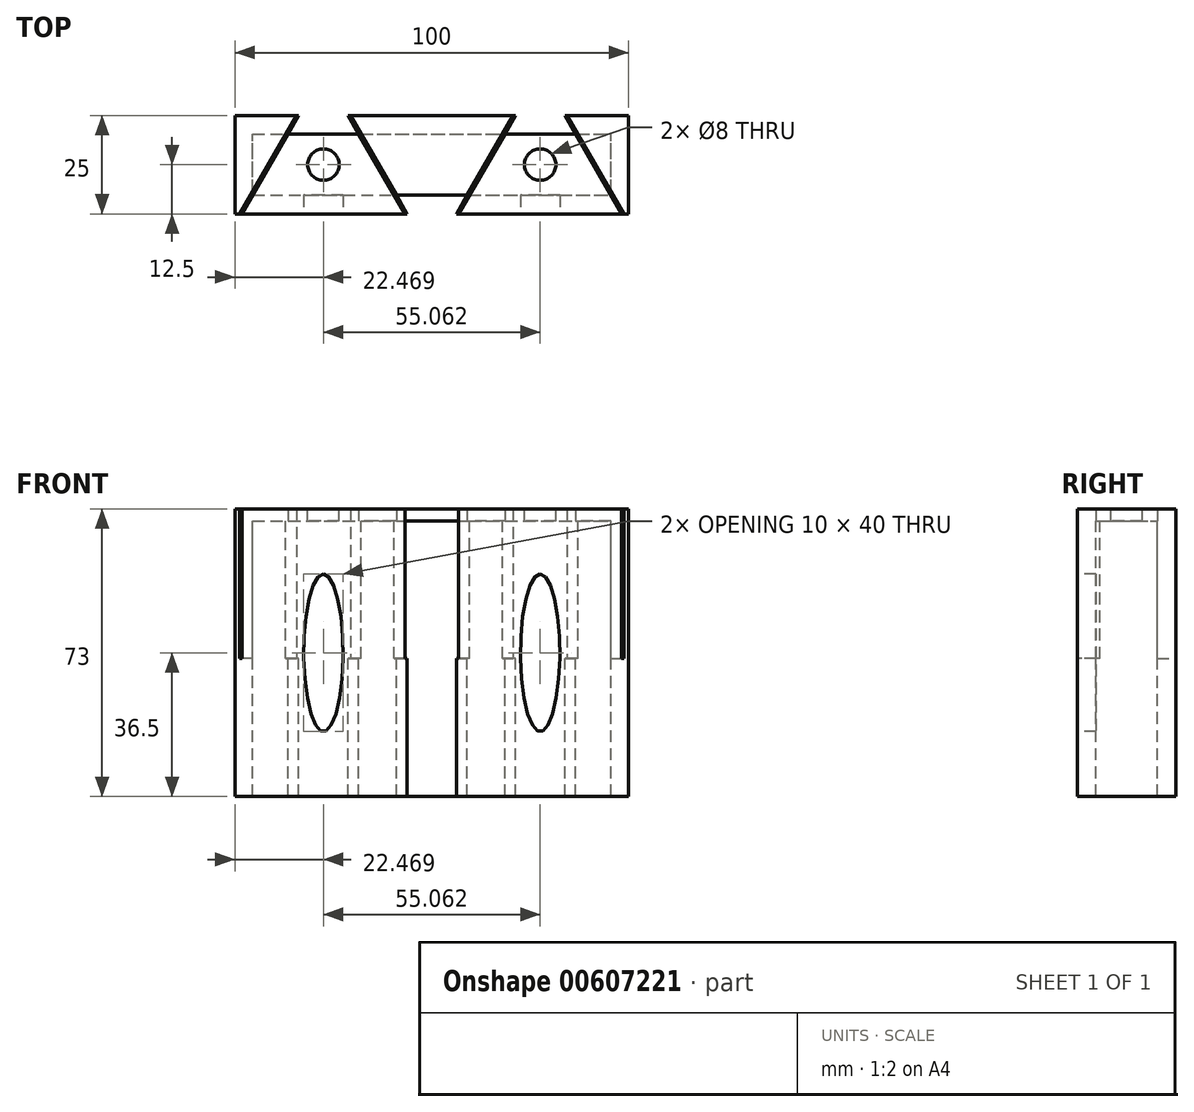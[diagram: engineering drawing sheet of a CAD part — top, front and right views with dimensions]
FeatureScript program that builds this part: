
annotation { "Feature Type Name" : "Feature", "Feature Type Description" : "" }
export const myFeature = defineFeature(function(context is Context, id is Id, definition is map)
    precondition{}
    {
        {
            var Q0;
            Q0=qCreatedBy(makeId("Top.planeOp"),FACE);
            var sketch = newSketch(context, id + "F0", { "sketchPlane" : qUnion([Q0])});
            skLineSegment(sketch, "E0.bottom", {"start": v(-45.5, -7.78) * mm, "end": v(45.5, -7.78) * mm});
            skLineSegment(sketch, "E0.top", {"start": v(-45.5, 7.78) * mm, "end": v(45.5, 7.78) * mm});
            skLineSegment(sketch, "E0.left", {"start": v(-45.5, -7.78) * mm, "end": v(-45.5, 7.78) * mm});
            skLineSegment(sketch, "E0.right", {"start": v(45.5, -7.78) * mm, "end": v(45.5, 7.78) * mm});
            skPoint(sketch, "E0.middle", {"position": v(0, 0) * mm});
            skLineSegment(sketch, "E1", {"start": v(-45.5, -7.78) * mm, "end": v(-36.52, 7.78) * mm});
            skLineSegment(sketch, "E2", {"start": v(-45.5, -6.78) * mm, "end": v(-37.1, 7.78) * mm});
            skLineSegment(sketch, "E3", {"start": v(-9.56, -7.78) * mm, "end": v(-18.55, 7.78) * mm});
            skLineSegment(sketch, "E4", {"start": v(-8.98, -7.78) * mm, "end": v(-17.97, 7.78) * mm});
            skLineSegment(sketch, "E5", {"start": v(8.98, -7.78) * mm, "end": v(17.97, 7.78) * mm});
            skLineSegment(sketch, "E6", {"start": v(9.56, -7.78) * mm, "end": v(18.55, 7.78) * mm});
            skLineSegment(sketch, "E7", {"start": v(45.5, -7.78) * mm, "end": v(36.52, 7.78) * mm});
            skLineSegment(sketch, "E8", {"start": v(45.5, -6.78) * mm, "end": v(37.1, 7.78) * mm});
            skLineSegment(sketch, "E9", {"start": v(-36.52, 7.78) * mm, "end": v(-18.55, 7.78) * mm});
            skLineSegment(sketch, "E10", {"start": v(-8.98, -7.78) * mm, "end": v(8.98, -7.78) * mm});
            skLineSegment(sketch, "E11", {"start": v(18.55, 7.78) * mm, "end": v(36.52, 7.78) * mm});
            skLineSegment(sketch, "E12.bottom", {"start": v(-50, -12.5) * mm, "end": v(50, -12.5) * mm});
            skLineSegment(sketch, "E12.top", {"start": v(-50, 12.5) * mm, "end": v(50, 12.5) * mm});
            skLineSegment(sketch, "E12.left", {"start": v(-50, -12.5) * mm, "end": v(-50, 12.5) * mm});
            skLineSegment(sketch, "E12.right", {"start": v(50, -12.5) * mm, "end": v(50, 12.5) * mm});
            skLineSegment(sketch, "E13", {"start": v(-45.5, -6.78) * mm, "end": v(-48.8, -12.5) * mm});
            skLineSegment(sketch, "E14", {"start": v(-45.5, -7.78) * mm, "end": v(-48.22, -12.5) * mm});
            skLineSegment(sketch, "E15", {"start": v(-37.1, 7.78) * mm, "end": v(-34.37, 12.5) * mm});
            skLineSegment(sketch, "E16", {"start": v(-36.52, 7.78) * mm, "end": v(-33.8, 12.5) * mm});
            skLineSegment(sketch, "E17", {"start": v(-18.55, 7.78) * mm, "end": v(-21.27, 12.5) * mm});
            skLineSegment(sketch, "E18", {"start": v(-17.97, 7.78) * mm, "end": v(-20.7, 12.5) * mm});
            skLineSegment(sketch, "E19", {"start": v(-9.56, -7.78) * mm, "end": v(-6.84, -12.5) * mm});
            skLineSegment(sketch, "E20", {"start": v(-8.98, -7.78) * mm, "end": v(-6.26, -12.5) * mm});
            skLineSegment(sketch, "E21", {"start": v(17.97, 7.78) * mm, "end": v(20.7, 12.5) * mm});
            skLineSegment(sketch, "E22", {"start": v(18.55, 7.78) * mm, "end": v(21.27, 12.5) * mm});
            skLineSegment(sketch, "E23", {"start": v(8.98, -7.78) * mm, "end": v(6.26, -12.5) * mm});
            skLineSegment(sketch, "E24", {"start": v(9.56, -7.78) * mm, "end": v(6.84, -12.5) * mm});
            skLineSegment(sketch, "E25", {"start": v(36.52, 7.78) * mm, "end": v(33.8, 12.5) * mm});
            skLineSegment(sketch, "E26", {"start": v(37.1, 7.78) * mm, "end": v(34.37, 12.5) * mm});
            skLineSegment(sketch, "E27", {"start": v(45.5, -7.78) * mm, "end": v(48.22, -12.5) * mm});
            skLineSegment(sketch, "E28", {"start": v(45.5, -6.78) * mm, "end": v(48.8, -12.5) * mm});
            skSolve(sketch);
        }
        {
            var Q0;
            Q0=makeQuery(id+"F0.imprint","IMPRINT",FACE,{"disambiguationData":[TD([[makeQuery(id+"F0.imprint","IMPRINT",EDGE,{"derivedFrom":sQuery(id+"F0.wireOp",EDGE,"E10")}),-1.0]])]});
            var Q1;
            {var subQ3=sQuery(id+"F0.wireOp",EDGE,"E2");Q1=makeQuery(id+"F0.imprint","IMPRINT",FACE,{"disambiguationData":[TD([[makeQuery(id+"F0.imprint","IMPRINT",EDGE,{"derivedFrom":subQ3}),1.0]])]});}
            var Q2;
            {var subQ3=sQuery(id+"F0.wireOp",EDGE,"E8");Q2=makeQuery(id+"F0.imprint","IMPRINT",FACE,{"disambiguationData":[TD([[makeQuery(id+"F0.imprint","IMPRINT",EDGE,{"derivedFrom":subQ3}),-1.0]])]});}
            var Q3;
            Q3=makeQuery(id+"F0.imprint","IMPRINT",FACE,{"disambiguationData":[TD([[makeQuery(id+"F0.imprint","IMPRINT",EDGE,{"derivedFrom":sQuery(id+"F0.wireOp",EDGE,"E11")}),1.0]])]});
            var Q4;
            {var subQ2=sQuery(id+"F0.wireOp",EDGE,"E24");Q4=makeQuery(id+"F0.imprint","IMPRINT",FACE,{"disambiguationData":[TD([[makeQuery(id+"F0.imprint","IMPRINT",EDGE,{"derivedFrom":subQ2}),1.0]])]});}
            var Q5;
            {var subQ0=sQuery(id+"F0.wireOp",EDGE,"E12.left");Q5=makeQuery(id+"F0.imprint","IMPRINT",FACE,{"disambiguationData":[TD([[makeQuery(id+"F0.imprint","IMPRINT",EDGE,{"derivedFrom":subQ0}),-1.0]])]});}
            var Q6;
            {var subQ0=sQuery(id+"F0.wireOp",EDGE,"E18");Q6=makeQuery(id+"F0.imprint","IMPRINT",FACE,{"disambiguationData":[TD([[makeQuery(id+"F0.imprint","IMPRINT",EDGE,{"derivedFrom":subQ0}),-1.0]])]});}
            var Q7;
            {var subQ0=sQuery(id+"F0.wireOp",EDGE,"E12.right");Q7=makeQuery(id+"F0.imprint","IMPRINT",FACE,{"disambiguationData":[TD([[makeQuery(id+"F0.imprint","IMPRINT",EDGE,{"derivedFrom":subQ0}),1.0]])]});}
            var Q8;
            {var subQ0=sQuery(id+"F0.wireOp",EDGE,"E4");Q8=makeQuery(id+"F0.imprint","IMPRINT",FACE,{"disambiguationData":[TD([[makeQuery(id+"F0.imprint","IMPRINT",EDGE,{"derivedFrom":subQ0}),-1.0]])]});}
            var Q9;
            {var subQ2=sQuery(id+"F0.wireOp",EDGE,"E6");Q9=makeQuery(id+"F0.imprint","IMPRINT",FACE,{"disambiguationData":[TD([[makeQuery(id+"F0.imprint","IMPRINT",EDGE,{"derivedFrom":subQ2}),-1.0]])]});}
            var Q10;
            {var subQ0=sQuery(id+"F0.wireOp",EDGE,"E1");Q10=makeQuery(id+"F0.imprint","IMPRINT",FACE,{"disambiguationData":[TD([[makeQuery(id+"F0.imprint","IMPRINT",EDGE,{"derivedFrom":subQ0}),-1.0]])]});}
            var Q11;
            Q11=makeQuery(id+"F0.imprint","IMPRINT",FACE,{"disambiguationData":[TD([[makeQuery(id+"F0.imprint","IMPRINT",EDGE,{"derivedFrom":sQuery(id+"F0.wireOp",EDGE,"E9")}),1.0]])]});
            var Q12;
            {var subQ0=sQuery(id+"F0.wireOp",EDGE,"E14");Q12=makeQuery(id+"F0.imprint","IMPRINT",FACE,{"disambiguationData":[TD([[makeQuery(id+"F0.imprint","IMPRINT",EDGE,{"derivedFrom":subQ0}),1.0]])]});}
            extrude(context, id + "F1", {"entities" : qUnion([Q0, Q1, Q2, Q3, Q4, Q5, Q6, Q7, Q8, Q9, Q10, Q11, Q12]), "depth" : 3 * mm, "offsetDistance" : 25 * mm});
        }
        {
            var Q0;
            {var subQ0=sQuery(id+"F0.wireOp",EDGE,"E12.left");Q0=makeQuery(id+"F0.imprint","IMPRINT",FACE,{"disambiguationData":[TD([[makeQuery(id+"F0.imprint","IMPRINT",EDGE,{"derivedFrom":subQ0}),-1.0]])]});}
            var Q1;
            {var subQ0=sQuery(id+"F0.wireOp",EDGE,"E14");Q1=makeQuery(id+"F0.imprint","IMPRINT",FACE,{"disambiguationData":[TD([[makeQuery(id+"F0.imprint","IMPRINT",EDGE,{"derivedFrom":subQ0}),1.0]])]});}
            var Q2;
            {var subQ0=sQuery(id+"F0.wireOp",EDGE,"E18");Q2=makeQuery(id+"F0.imprint","IMPRINT",FACE,{"disambiguationData":[TD([[makeQuery(id+"F0.imprint","IMPRINT",EDGE,{"derivedFrom":subQ0}),-1.0]])]});}
            var Q3;
            Q3=makeQuery(id+"F0.imprint","IMPRINT",FACE,{"disambiguationData":[TD([[makeQuery(id+"F0.imprint","IMPRINT",EDGE,{"derivedFrom":sQuery(id+"F0.wireOp",EDGE,"E10")}),-1.0]])]});
            var Q4;
            {var subQ2=sQuery(id+"F0.wireOp",EDGE,"E24");Q4=makeQuery(id+"F0.imprint","IMPRINT",FACE,{"disambiguationData":[TD([[makeQuery(id+"F0.imprint","IMPRINT",EDGE,{"derivedFrom":subQ2}),1.0]])]});}
            var Q5;
            Q5=makeQuery(id+"F0.imprint","IMPRINT",FACE,{"disambiguationData":[TD([[makeQuery(id+"F0.imprint","IMPRINT",EDGE,{"derivedFrom":sQuery(id+"F0.wireOp",EDGE,"E11")}),1.0]])]});
            var Q6;
            {var subQ0=sQuery(id+"F0.wireOp",EDGE,"E12.right");Q6=makeQuery(id+"F0.imprint","IMPRINT",FACE,{"disambiguationData":[TD([[makeQuery(id+"F0.imprint","IMPRINT",EDGE,{"derivedFrom":subQ0}),1.0]])]});}
            var Q7;
            Q7=makeQuery(id+"F0.imprint","IMPRINT",FACE,{"disambiguationData":[TD([[makeQuery(id+"F0.imprint","IMPRINT",EDGE,{"derivedFrom":sQuery(id+"F0.wireOp",EDGE,"E9")}),1.0]])]});
            extrude(context, id + "F2", {"entities" : qUnion([Q0, Q1, Q2, Q3, Q4, Q5, Q6, Q7]), "operationType" : NewBodyOperationType.ADD, "oppositeDirection" : true, "depth" : 35 * mm, "offsetDistance" : 25 * mm});
        }
        {
            var Q0;
            {var subQ0=sQuery(id+"F0.wireOp",EDGE,"E19");Q0=makeQuery(id+"F0.imprint","IMPRINT",FACE,{"disambiguationData":[TD([[makeQuery(id+"F0.imprint","IMPRINT",EDGE,{"derivedFrom":subQ0}),1.0]])]});}
            var Q1;
            Q1=makeQuery(id+"F0.imprint","IMPRINT",FACE,{"disambiguationData":[TD([[makeQuery(id+"F0.imprint","IMPRINT",EDGE,{"derivedFrom":sQuery(id+"F0.wireOp",EDGE,"E9")}),1.0]])]});
            var Q2;
            {var subQ2=sQuery(id+"F0.wireOp",EDGE,"E13");Q2=makeQuery(id+"F0.imprint","IMPRINT",FACE,{"disambiguationData":[TD([[makeQuery(id+"F0.imprint","IMPRINT",EDGE,{"derivedFrom":subQ2}),1.0]])]});}
            var Q3;
            {var subQ0=sQuery(id+"F0.wireOp",EDGE,"E27");Q3=makeQuery(id+"F0.imprint","IMPRINT",FACE,{"disambiguationData":[TD([[makeQuery(id+"F0.imprint","IMPRINT",EDGE,{"derivedFrom":subQ0}),1.0]])]});}
            var Q4;
            Q4=makeQuery(id+"F0.imprint","IMPRINT",FACE,{"disambiguationData":[TD([[makeQuery(id+"F0.imprint","IMPRINT",EDGE,{"derivedFrom":sQuery(id+"F0.wireOp",EDGE,"E10")}),-1.0]])]});
            var Q5;
            {var subQ0=sQuery(id+"F0.wireOp",EDGE,"E14");Q5=makeQuery(id+"F0.imprint","IMPRINT",FACE,{"disambiguationData":[TD([[makeQuery(id+"F0.imprint","IMPRINT",EDGE,{"derivedFrom":subQ0}),1.0]])]});}
            var Q6;
            {var subQ0=sQuery(id+"F0.wireOp",EDGE,"E23");Q6=makeQuery(id+"F0.imprint","IMPRINT",FACE,{"disambiguationData":[TD([[makeQuery(id+"F0.imprint","IMPRINT",EDGE,{"derivedFrom":subQ0}),1.0]])]});}
            var Q7;
            {var subQ2=sQuery(id+"F0.wireOp",EDGE,"E24");Q7=makeQuery(id+"F0.imprint","IMPRINT",FACE,{"disambiguationData":[TD([[makeQuery(id+"F0.imprint","IMPRINT",EDGE,{"derivedFrom":subQ2}),1.0]])]});}
            var Q8;
            {var subQ0=sQuery(id+"F0.wireOp",EDGE,"E12.left");Q8=makeQuery(id+"F0.imprint","IMPRINT",FACE,{"disambiguationData":[TD([[makeQuery(id+"F0.imprint","IMPRINT",EDGE,{"derivedFrom":subQ0}),-1.0]])]});}
            var Q9;
            {var subQ2=sQuery(id+"F0.wireOp",EDGE,"E15");Q9=makeQuery(id+"F0.imprint","IMPRINT",FACE,{"disambiguationData":[TD([[makeQuery(id+"F0.imprint","IMPRINT",EDGE,{"derivedFrom":subQ2}),-1.0]])]});}
            var Q10;
            {var subQ0=sQuery(id+"F0.wireOp",EDGE,"E17");Q10=makeQuery(id+"F0.imprint","IMPRINT",FACE,{"disambiguationData":[TD([[makeQuery(id+"F0.imprint","IMPRINT",EDGE,{"derivedFrom":subQ0}),-1.0]])]});}
            var Q11;
            {var subQ0=sQuery(id+"F0.wireOp",EDGE,"E18");Q11=makeQuery(id+"F0.imprint","IMPRINT",FACE,{"disambiguationData":[TD([[makeQuery(id+"F0.imprint","IMPRINT",EDGE,{"derivedFrom":subQ0}),-1.0]])]});}
            var Q12;
            {var subQ0=sQuery(id+"F0.wireOp",EDGE,"E21");Q12=makeQuery(id+"F0.imprint","IMPRINT",FACE,{"disambiguationData":[TD([[makeQuery(id+"F0.imprint","IMPRINT",EDGE,{"derivedFrom":subQ0}),-1.0]])]});}
            var Q13;
            {var subQ0=sQuery(id+"F0.wireOp",EDGE,"E25");Q13=makeQuery(id+"F0.imprint","IMPRINT",FACE,{"disambiguationData":[TD([[makeQuery(id+"F0.imprint","IMPRINT",EDGE,{"derivedFrom":subQ0}),-1.0]])]});}
            var Q14;
            {var subQ0=sQuery(id+"F0.wireOp",EDGE,"E12.right");Q14=makeQuery(id+"F0.imprint","IMPRINT",FACE,{"disambiguationData":[TD([[makeQuery(id+"F0.imprint","IMPRINT",EDGE,{"derivedFrom":subQ0}),1.0]])]});}
            var Q15;
            Q15=makeQuery(id+"F0.imprint","IMPRINT",FACE,{"disambiguationData":[TD([[makeQuery(id+"F0.imprint","IMPRINT",EDGE,{"derivedFrom":sQuery(id+"F0.wireOp",EDGE,"E11")}),1.0]])]});
            var Q16;
            Q16=makeQuery(id+"F2.opExtrude","CAP_FACE",FACE,{"disambiguationData":[OSD([sQuery(id+"F0.wireOp",EDGE,"E9"),sQuery(id+"F0.wireOp",EDGE,"E12.top"),sQuery(id+"F0.wireOp",EDGE,"E16"),sQuery(id+"F0.wireOp",EDGE,"E17")])],"isStart":false});
            extrude(context, id + "F3", {"entities" : qUnion([Q0, Q1, Q2, Q3, Q4, Q5, Q6, Q7, Q8, Q9, Q10, Q11, Q12, Q13, Q14, Q15]), "operationType" : NewBodyOperationType.ADD, "oppositeDirection" : true, "depth" : 70 * mm, "offsetDistance" : 25 * mm, "hasSecondDirection" : true, "secondDirectionBound" : SecondDirectionBoundingType.UP_TO_SURFACE, "secondDirectionOppositeDirection" : true, "secondDirectionDepth" : 25 * mm, "secondDirectionBoundEntityFace" : qUnion([Q16])});
        }
        {
            var Q0;
            {var subQ0=sQuery(id+"F0.wireOp",EDGE,"E12.bottom");var subQ1=makeQuery(id+"F0.imprint","IMPRINT",EDGE,{"disambiguationData":[TD([[makeQuery(id+"F0.imprint","INTERSECT",VERTEX,{"derivedFrom":[subQ0,sQuery(id+"F0.wireOp",EDGE,"E12.right")]}),1.0]])],"derivedFrom":subQ0});var subQ2=makeQuery(id+"F0.imprint","IMPRINT",EDGE,{"disambiguationData":[TD([[makeQuery(id+"F0.imprint","INTERSECT",VERTEX,{"derivedFrom":[subQ0,sQuery(id+"F0.wireOp",EDGE,"E24")]}),-1.0]])],"derivedFrom":subQ0});var subQ3=makeQuery(id+"F0.imprint","IMPRINT",EDGE,{"disambiguationData":[TD([[makeQuery(id+"F0.imprint","INTERSECT",VERTEX,{"derivedFrom":[subQ0,sQuery(id+"F0.wireOp",EDGE,"E20")]}),-1.0]])],"derivedFrom":subQ0});var subQ4=makeQuery(id+"F0.imprint","IMPRINT",EDGE,{"disambiguationData":[TD([[makeQuery(id+"F0.imprint","INTERSECT",VERTEX,{"derivedFrom":[subQ0,sQuery(id+"F0.wireOp",EDGE,"E14")]}),-1.0]])],"derivedFrom":subQ0});var subQ5=makeQuery(id+"F0.imprint","IMPRINT",EDGE,{"disambiguationData":[TD([[makeQuery(id+"F0.imprint","INTERSECT",VERTEX,{"derivedFrom":[subQ0,sQuery(id+"F0.wireOp",EDGE,"E12.left")]}),-1.0]])],"derivedFrom":subQ0});Q0=makeQuery(id+"F3.boolean.opBoolean","MERGE",FACE,{"derivedFrom":[makeQuery(id+"F2.boolean.opBoolean","MERGE",FACE,{"derivedFrom":[makeQuery(id+"F1.opExtrude","SWEPT_FACE",FACE,{"disambiguationData":[OSD([subQ0]),TDD([subQ5])]}),makeQuery(id+"F2.opExtrude","SWEPT_FACE",FACE,{"disambiguationData":[OSD([subQ0]),TDD([subQ5])]})]}),makeQuery(id+"F2.boolean.opBoolean","MERGE",FACE,{"derivedFrom":[makeQuery(id+"F1.opExtrude","SWEPT_FACE",FACE,{"disambiguationData":[OSD([subQ0]),TDD([subQ4])]}),makeQuery(id+"F2.opExtrude","SWEPT_FACE",FACE,{"disambiguationData":[OSD([subQ0]),TDD([subQ4])]})]}),makeQuery(id+"F2.boolean.opBoolean","MERGE",FACE,{"derivedFrom":[makeQuery(id+"F1.opExtrude","SWEPT_FACE",FACE,{"disambiguationData":[OSD([subQ0]),TDD([subQ3])]}),makeQuery(id+"F2.opExtrude","SWEPT_FACE",FACE,{"disambiguationData":[OSD([subQ0]),TDD([subQ3])]})]}),makeQuery(id+"F2.boolean.opBoolean","MERGE",FACE,{"derivedFrom":[makeQuery(id+"F1.opExtrude","SWEPT_FACE",FACE,{"disambiguationData":[OSD([subQ0]),TDD([subQ2])]}),makeQuery(id+"F2.opExtrude","SWEPT_FACE",FACE,{"disambiguationData":[OSD([subQ0]),TDD([subQ2])]})]}),makeQuery(id+"F2.boolean.opBoolean","MERGE",FACE,{"derivedFrom":[makeQuery(id+"F1.opExtrude","SWEPT_FACE",FACE,{"disambiguationData":[OSD([subQ0]),TDD([subQ1])]}),makeQuery(id+"F2.opExtrude","SWEPT_FACE",FACE,{"disambiguationData":[OSD([subQ0]),TDD([subQ1])]})]}),makeQuery(id+"F3.opExtrude","SWEPT_FACE",FACE,{"disambiguationData":[OSD([subQ0])]})]});}
            var sketch = newSketch(context, id + "F4", { "sketchPlane" : qUnion([Q0])});
            skLineSegment(sketch, "E29", {"start": v(-48.22, 3) * mm, "end": v(-6.84, -70) * mm, "construction": true});
            skEllipse(sketch, "E30", {"center": v(-27.53, -33.5) * mm, "majorRadius": 20 * mm, "minorRadius": 5 * mm, "majorAxis": v(0, 1)});
            skLineSegment(sketch, "E31", {"start": v(0, 3) * mm, "end": v(0, -70) * mm, "construction": true});
            skEllipse(sketch, "E32.MirrorC", {"center": v(27.53, -33.5) * mm, "majorRadius": 20 * mm, "minorRadius": 5 * mm, "majorAxis": v(0, 1)});
            skSolve(sketch);
        }
        {
            var Q0;
            Q0=makeQuery(id+"F4.imprint","IMPRINT",FACE,{"disambiguationData":[TD([[makeQuery(id+"F4.imprint","IMPRINT",EDGE,{"derivedFrom":sQuery(id+"F4.wireOp",EDGE,"E30")}),1.0]])]});
            var Q1;
            Q1=makeQuery(id+"F4.imprint","IMPRINT",FACE,{"disambiguationData":[TD([[makeQuery(id+"F4.imprint","IMPRINT",EDGE,{"derivedFrom":sQuery(id+"F4.wireOp",EDGE,"E32.MirrorC")}),1.0]])]});
            extrude(context, id + "F5", {"entities" : qUnion([Q0, Q1]), "operationType" : NewBodyOperationType.REMOVE, "endBound" : BoundingType.UP_TO_NEXT, "oppositeDirection" : true, "depth" : 25 * mm, "offsetDistance" : 25 * mm});
        }
        {
            var Q0;
            Q0=makeQuery(id+"F1.opExtrude","CAP_FACE",FACE,{"disambiguationData":[OSD([sQuery(id+"F0.wireOp",EDGE,"E1"),sQuery(id+"F0.wireOp",EDGE,"E3"),sQuery(id+"F0.wireOp",EDGE,"E12.bottom"),sQuery(id+"F0.wireOp",EDGE,"E12.top"),sQuery(id+"F0.wireOp",EDGE,"E14"),sQuery(id+"F0.wireOp",EDGE,"E16"),sQuery(id+"F0.wireOp",EDGE,"E17"),sQuery(id+"F0.wireOp",EDGE,"E19")])],"isStart":false});
            var sketch = newSketch(context, id + "F6", { "sketchPlane" : qUnion([Q0])});
            skLineSegment(sketch, "E33", {"start": v(-50, 0) * mm, "end": v(50, 0) * mm});
            skCircle(sketch, "E34", {"center": v(-27.53, 0) * mm, "radius": 4 * mm});
            skPoint(sketch, "E34.centerSnap0", {"position": v(-27.53, 12.5) * mm});
            skCircle(sketch, "E35", {"center": v(0, 0) * mm, "radius": 4 * mm});
            skCircle(sketch, "E36", {"center": v(27.53, 0) * mm, "radius": 4 * mm});
            skLineSegment(sketch, "E37", {"start": v(27.53, 12.5) * mm, "end": v(27.53, -12.5) * mm});
            skSolve(sketch);
        }
        {
            var Q0;
            {var subQ0=sQuery(id+"F6.wireOp",EDGE,"E34");var subQ1=sQuery(id+"F6.wireOp",EDGE,"E33");var subQ2=makeQuery(id+"F6.imprint","INTERSECT",VERTEX,{"disambiguationData":[OD(0.0)],"derivedFrom":[subQ1,subQ0]});Q0=makeQuery(id+"F6.imprint","IMPRINT",FACE,{"disambiguationData":[TD([[makeQuery(id+"F6.imprint","IMPRINT",EDGE,{"disambiguationData":[TD([[subQ2,-1.0]])],"derivedFrom":subQ1}),1.0]])]});}
            var Q1;
            {var subQ0=sQuery(id+"F6.wireOp",EDGE,"E34");var subQ1=sQuery(id+"F6.wireOp",EDGE,"E33");var subQ2=makeQuery(id+"F6.imprint","INTERSECT",VERTEX,{"disambiguationData":[OD(0.0)],"derivedFrom":[subQ1,subQ0]});Q1=makeQuery(id+"F6.imprint","IMPRINT",FACE,{"disambiguationData":[TD([[makeQuery(id+"F6.imprint","IMPRINT",EDGE,{"disambiguationData":[TD([[subQ2,-1.0]])],"derivedFrom":subQ1}),-1.0]])]});}
            var Q2;
            {var subQ0=sQuery(id+"F6.wireOp",EDGE,"E35");var subQ1=sQuery(id+"F6.wireOp",EDGE,"E33");var subQ2=makeQuery(id+"F6.imprint","INTERSECT",VERTEX,{"disambiguationData":[OD(0.0)],"derivedFrom":[subQ1,subQ0]});Q2=makeQuery(id+"F6.imprint","IMPRINT",FACE,{"disambiguationData":[TD([[makeQuery(id+"F6.imprint","IMPRINT",EDGE,{"disambiguationData":[TD([[subQ2,-1.0]])],"derivedFrom":subQ1}),-1.0]])]});}
            var Q3;
            {var subQ0=sQuery(id+"F6.wireOp",EDGE,"E35");var subQ1=sQuery(id+"F6.wireOp",EDGE,"E33");var subQ2=makeQuery(id+"F6.imprint","INTERSECT",VERTEX,{"disambiguationData":[OD(0.0)],"derivedFrom":[subQ1,subQ0]});Q3=makeQuery(id+"F6.imprint","IMPRINT",FACE,{"disambiguationData":[TD([[makeQuery(id+"F6.imprint","IMPRINT",EDGE,{"disambiguationData":[TD([[subQ2,-1.0]])],"derivedFrom":subQ1}),1.0]])]});}
            var Q4;
            {var subQ0=sQuery(id+"F6.wireOp",EDGE,"E36");var subQ1=sQuery(id+"F6.wireOp",EDGE,"E33");var subQ2=makeQuery(id+"F6.imprint","INTERSECT",VERTEX,{"disambiguationData":[OD(1.0)],"derivedFrom":[subQ1,subQ0]});Q4=makeQuery(id+"F6.imprint","IMPRINT",FACE,{"disambiguationData":[TD([[makeQuery(id+"F6.imprint","IMPRINT",EDGE,{"disambiguationData":[TD([[subQ2,1.0]])],"derivedFrom":subQ1}),-1.0]])]});}
            var Q5;
            {var subQ0=sQuery(id+"F6.wireOp",EDGE,"E36");var subQ1=sQuery(id+"F6.wireOp",EDGE,"E33");var subQ2=makeQuery(id+"F6.imprint","INTERSECT",VERTEX,{"disambiguationData":[OD(0.0)],"derivedFrom":[subQ1,subQ0]});Q5=makeQuery(id+"F6.imprint","IMPRINT",FACE,{"disambiguationData":[TD([[makeQuery(id+"F6.imprint","IMPRINT",EDGE,{"disambiguationData":[TD([[subQ2,-1.0]])],"derivedFrom":subQ1}),-1.0]])]});}
            var Q6;
            {var subQ0=sQuery(id+"F6.wireOp",EDGE,"E36");var subQ1=sQuery(id+"F6.wireOp",EDGE,"E33");var subQ2=makeQuery(id+"F6.imprint","INTERSECT",VERTEX,{"disambiguationData":[OD(0.0)],"derivedFrom":[subQ1,subQ0]});Q6=makeQuery(id+"F6.imprint","IMPRINT",FACE,{"disambiguationData":[TD([[makeQuery(id+"F6.imprint","IMPRINT",EDGE,{"disambiguationData":[TD([[subQ2,-1.0]])],"derivedFrom":subQ1}),1.0]])]});}
            var Q7;
            {var subQ0=sQuery(id+"F6.wireOp",EDGE,"E36");var subQ1=sQuery(id+"F6.wireOp",EDGE,"E33");var subQ2=makeQuery(id+"F6.imprint","INTERSECT",VERTEX,{"disambiguationData":[OD(1.0)],"derivedFrom":[subQ1,subQ0]});Q7=makeQuery(id+"F6.imprint","IMPRINT",FACE,{"disambiguationData":[TD([[makeQuery(id+"F6.imprint","IMPRINT",EDGE,{"disambiguationData":[TD([[subQ2,1.0]])],"derivedFrom":subQ1}),1.0]])]});}
            extrude(context, id + "F7", {"entities" : qUnion([Q0, Q1, Q2, Q3, Q4, Q5, Q6, Q7]), "operationType" : NewBodyOperationType.REMOVE, "endBound" : BoundingType.UP_TO_NEXT, "oppositeDirection" : true, "depth" : 25 * mm, "offsetDistance" : 25 * mm});
        }
    });
